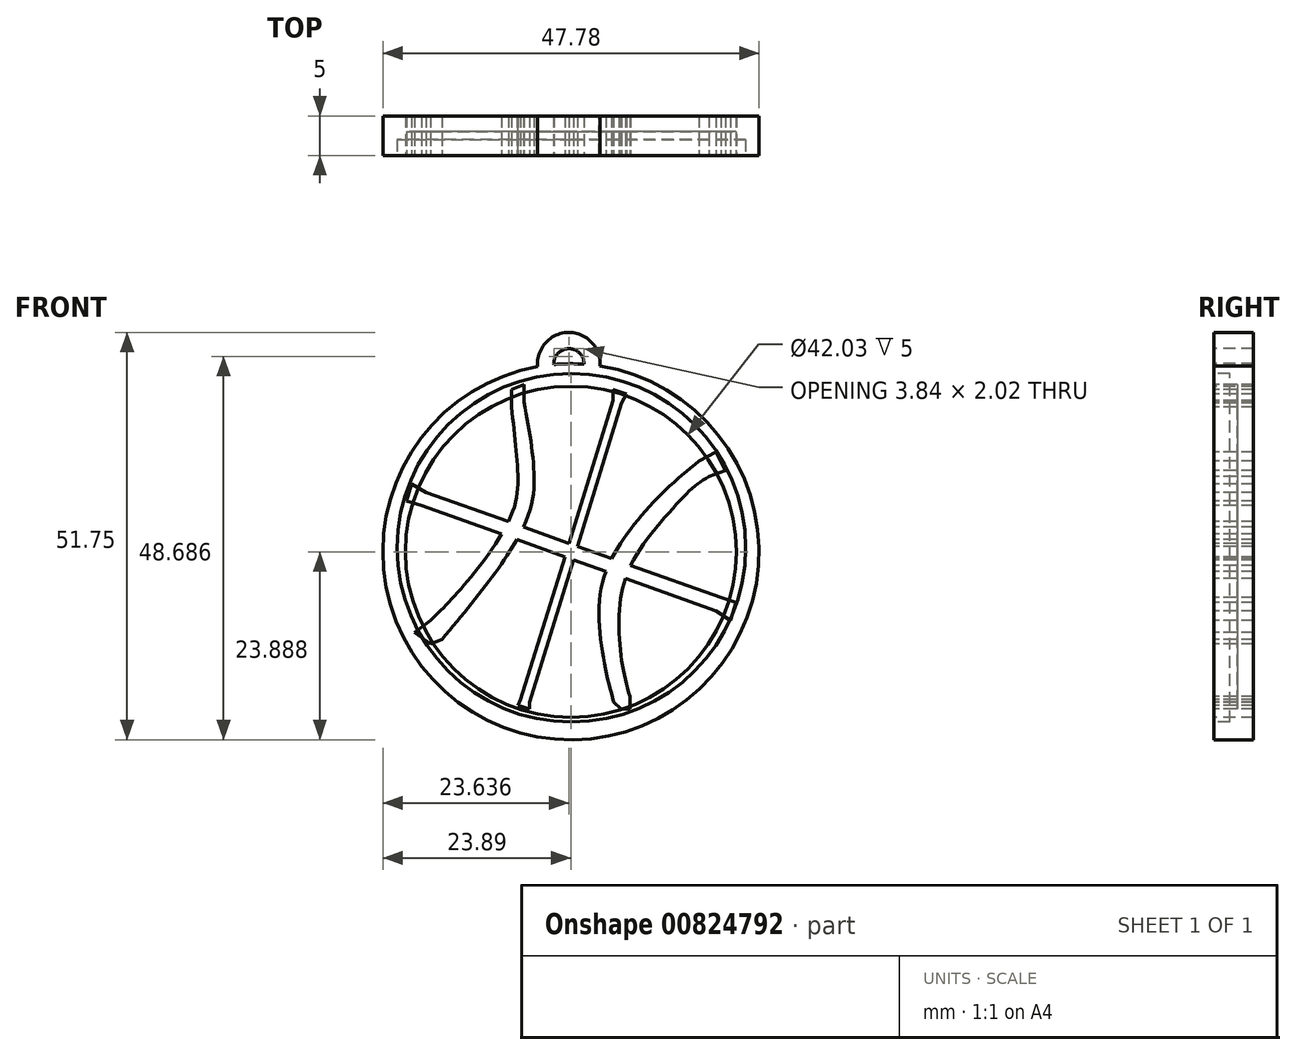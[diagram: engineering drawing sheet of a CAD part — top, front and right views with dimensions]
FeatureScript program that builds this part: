
annotation { "Feature Type Name" : "Feature", "Feature Type Description" : "" }
export const myFeature = defineFeature(function(context is Context, id is Id, definition is map)
    precondition{}
    {
        {
            var Q0;
            Q0=qCreatedBy(makeId("Front.planeOp"),FACE);
            var sketch = newSketch(context, id + "F0", { "sketchPlane" : qUnion([Q0])});
            skCircle(sketch, "E0", {"center": v(-21, 21.85) * mm, "radius": 21.02 * mm});
            skLineSegment(sketch, "E1", {"start": v(-21.37, 21.46) * mm, "end": v(-21.18, 22.04) * mm});
            skArc(sketch, "E2", {"start": v(-19.34, 45.68) * mm, "mid": v(-21.26, 45.73) * mm, "end": v(-23.17, 45.64) * mm});
            skPoint(sketch, "E3.center.orphan", {"position": v(-21.18, 43.7) * mm});
            skArc(sketch, "E4", {"start": v(-19.34, 45.68) * mm, "mid": v(-21.28, 47.65) * mm, "end": v(-23.17, 45.64) * mm});
            skArc(sketch, "E5", {"start": v(-17.29, 45.45) * mm, "mid": v(-21.3, 49.71) * mm, "end": v(-25.21, 45.36) * mm});
            skArc(sketch, "E6.trimOffspring", {"start": v(-25.21, 45.36) * mm, "mid": v(-20.74, -2.04) * mm, "end": v(-17.29, 45.45) * mm});
            skLineSegment(sketch, "E7.trimOffspring", {"start": v(-21.18, 22.04) * mm, "end": v(-21, 21.85) * mm, "construction": true});
            skLineSegment(sketch, "E8.trimOffspring", {"start": v(-21.37, 21.46) * mm, "end": v(-21, 21.85) * mm, "construction": true});
            skSolve(sketch);
        }
        {
            var Q0;
            Q0=makeQuery(id+"F0.imprint","IMPRINT",FACE,{"disambiguationData":[TD([[makeQuery(id+"F0.imprint","IMPRINT",EDGE,{"derivedFrom":sQuery(id+"F0.wireOp",EDGE,"E0")}),1.0]])]});
            var sketch = newSketch(context, id + "F1", { "sketchPlane" : qUnion([Q0])});
            skLineSegment(sketch, "E9", {"start": v(-15.64, 41.06) * mm, "end": v(-21.24, 22.92) * mm});
            skLineSegment(sketch, "E10", {"start": v(-26.26, 2.72) * mm, "end": v(-20.68, 20.83) * mm});
            skLineSegment(sketch, "E11", {"start": v(-39.97, 27.73) * mm, "end": v(-29.8, 24.1) * mm});
            skLineSegment(sketch, "E12", {"start": v(-1.95, 16.02) * mm, "end": v(-13.4, 20.12) * mm});
            skFitSpline(sketch, "E13", {"points": [v(-26.93, 40.86) * mm, v(-25.75, 32.96) * mm, v(-26.76, 25.59) * mm, v(-37.39, 10.69) * mm], "startDerivative": vector(5.08, -28.06) * mm, "endDerivative": vector(-30.46, -36.74) * mm});
            skFitSpline(sketch, "E14", {"points": [v(-28.56, 40.27) * mm, v(-27.77, 32.34) * mm, v(-28.62, 26.36) * mm, v(-34.92, 17.2) * mm, v(-38.82, 13.14) * mm], "startDerivative": vector(3.84, -32.4) * mm, "endDerivative": vector(-16.35, -15.87) * mm});
            skFitSpline(sketch, "E15", {"points": [v(-4.73, 33.4) * mm, v(-9.64, 29.05) * mm, v(-14.35, 23.42) * mm, v(-17.21, 16.86) * mm, v(-16.84, 8.18) * mm, v(-15.56, 2.75) * mm], "startDerivative": vector(-25.64, -21.38) * mm, "endDerivative": vector(7.63, -28) * mm});
            skFitSpline(sketch, "E16", {"points": [v(-3.48, 31.4) * mm, v(-5.2, 30.25) * mm, v(-7.52, 27.94) * mm, v(-12.32, 22.03) * mm, v(-14.63, 16.12) * mm, v(-14.63, 8.55) * mm, v(-13.51, 3.44) * mm], "startDerivative": vector(-16.38, -9.76) * mm, "endDerivative": vector(7.6, -28.1) * mm});
            skPoint(sketch, "E17.0.internal.orphan", {"position": v(-43.17, 40.72) * mm});
            skLineSegment(sketch, "E18", {"start": v(-28.56, 40.27) * mm, "end": v(-28.56, 42.44) * mm});
            skLineSegment(sketch, "E19", {"start": v(-26.93, 40.86) * mm, "end": v(-26.93, 43.09) * mm});
            skLineSegment(sketch, "E20", {"start": v(-26.93, 43.09) * mm, "end": v(-28.56, 42.44) * mm});
            skLineSegment(sketch, "E21", {"start": v(-38.82, 13.14) * mm, "end": v(-40.9, 11.61) * mm});
            skLineSegment(sketch, "E22", {"start": v(-40.9, 11.61) * mm, "end": v(-38.82, 10.15) * mm});
            skLineSegment(sketch, "E23", {"start": v(-38.82, 10.15) * mm, "end": v(-37.39, 10.69) * mm});
            skLineSegment(sketch, "E24", {"start": v(-39.97, 27.73) * mm, "end": v(-41.89, 28.32) * mm});
            skLineSegment(sketch, "E25", {"start": v(-41.89, 28.32) * mm, "end": v(-41.22, 30.48) * mm});
            skLineSegment(sketch, "E26", {"start": v(-41.22, 30.48) * mm, "end": v(-39.37, 29.4) * mm});
            skLineSegment(sketch, "E27", {"start": v(-1.95, 16.02) * mm, "end": v(0, 15.42) * mm});
            skLineSegment(sketch, "E28", {"start": v(0, 15.42) * mm, "end": v(-0.7, 13.14) * mm});
            skLineSegment(sketch, "E29", {"start": v(-0.7, 13.14) * mm, "end": v(-2.55, 14.35) * mm});
            skLineSegment(sketch, "E30", {"start": v(-13.51, 3.44) * mm, "end": v(-13.51, 1.88) * mm});
            skLineSegment(sketch, "E31", {"start": v(-13.51, 1.88) * mm, "end": v(-14.63, 1.9) * mm});
            skLineSegment(sketch, "E32", {"start": v(-14.63, 1.9) * mm, "end": v(-15.56, 2.75) * mm});
            skLineSegment(sketch, "E33", {"start": v(-4.73, 33.4) * mm, "end": v(-2.55, 34.52) * mm});
            skLineSegment(sketch, "E34", {"start": v(-2.55, 34.52) * mm, "end": v(-1.35, 32.17) * mm});
            skLineSegment(sketch, "E35", {"start": v(-1.35, 32.17) * mm, "end": v(-3.48, 31.4) * mm});
            skLineSegment(sketch, "E36", {"start": v(-26.26, 2.72) * mm, "end": v(-26.26, 1.9) * mm});
            skLineSegment(sketch, "E37", {"start": v(-26.26, 1.9) * mm, "end": v(-27.73, 2.35) * mm});
            skLineSegment(sketch, "E38", {"start": v(-27.73, 2.35) * mm, "end": v(-27.37, 3.06) * mm});
            skLineSegment(sketch, "E39", {"start": v(-15.64, 41.06) * mm, "end": v(-15.64, 42.44) * mm});
            skLineSegment(sketch, "E40", {"start": v(-15.64, 42.44) * mm, "end": v(-13.94, 41.9) * mm});
            skLineSegment(sketch, "E41", {"start": v(-13.94, 41.9) * mm, "end": v(-14.54, 40.72) * mm});
            skFitSpline(sketch, "E42.trimOffspring", {"points": [v(-28.56, 40.27) * mm, v(-27.77, 32.34) * mm, v(-28.62, 26.36) * mm, v(-34.92, 17.2) * mm, v(-38.82, 13.14) * mm], "startDerivative": vector(3.84, -32.4) * mm, "endDerivative": vector(-16.35, -15.87) * mm});
            skLineSegment(sketch, "E43.trimOffspring", {"start": v(-28.94, 25.68) * mm, "end": v(-39.37, 29.4) * mm});
            skLineSegment(sketch, "E44.trimOffspring", {"start": v(-27.85, 23.4) * mm, "end": v(-21.76, 21.22) * mm});
            skLineSegment(sketch, "E45.trimOffspring", {"start": v(-21.76, 21.22) * mm, "end": v(-27.37, 3.06) * mm});
            skLineSegment(sketch, "E46.trimOffspring", {"start": v(-20.15, 22.53) * mm, "end": v(-14.54, 40.72) * mm});
            skLineSegment(sketch, "E47.trimOffspring", {"start": v(-21.24, 22.92) * mm, "end": v(-27.03, 25) * mm});
            skLineSegment(sketch, "E48.trimOffspring", {"start": v(-20.68, 20.83) * mm, "end": v(-16.54, 19.35) * mm});
            skLineSegment(sketch, "E49.trimOffspring", {"start": v(-14.07, 18.47) * mm, "end": v(-2.55, 14.35) * mm});
            skLineSegment(sketch, "E50.trimOffspring", {"start": v(-15.82, 20.98) * mm, "end": v(-20.15, 22.53) * mm});
            skSolve(sketch);
        }
        {
            var Q0;
            Q0 = qSketchRegion(id + "F0", true);
            var Q1;
            Q1 = qSketchRegion(id + "F1", true);
            extrude(context, id + "F2", {"entities" : qUnion([Q0, Q1]), "oppositeDirection" : true, "depth" : 5 * mm, "offsetDistance" : 25 * mm});
        }
        {
            var Q0;
            Q0 = qSketchRegion(id + "F1", true);
            extrude(context, id + "F3", {"entities" : qUnion([Q0]), "oppositeDirection" : true, "depth" : 3 * mm, "offsetDistance" : 25 * mm});
        }
        {
            var Q0;
            Q0=qCreatedBy(makeId("Front.planeOp"),FACE);
            var sketch = newSketch(context, id + "F4", { "sketchPlane" : qUnion([Q0])});
            skCircle(sketch, "E51", {"center": v(-20.93, 22.35) * mm, "radius": 22.14 * mm});
            skSolve(sketch);
        }
        {
            var Q0;
            Q0 = qSketchRegion(id + "F4", true);
            extrude(context, id + "F5", {"entities" : qUnion([Q0]), "oppositeDirection" : true, "depth" : 2 * mm, "offsetDistance" : 25 * mm});
        }
    });
